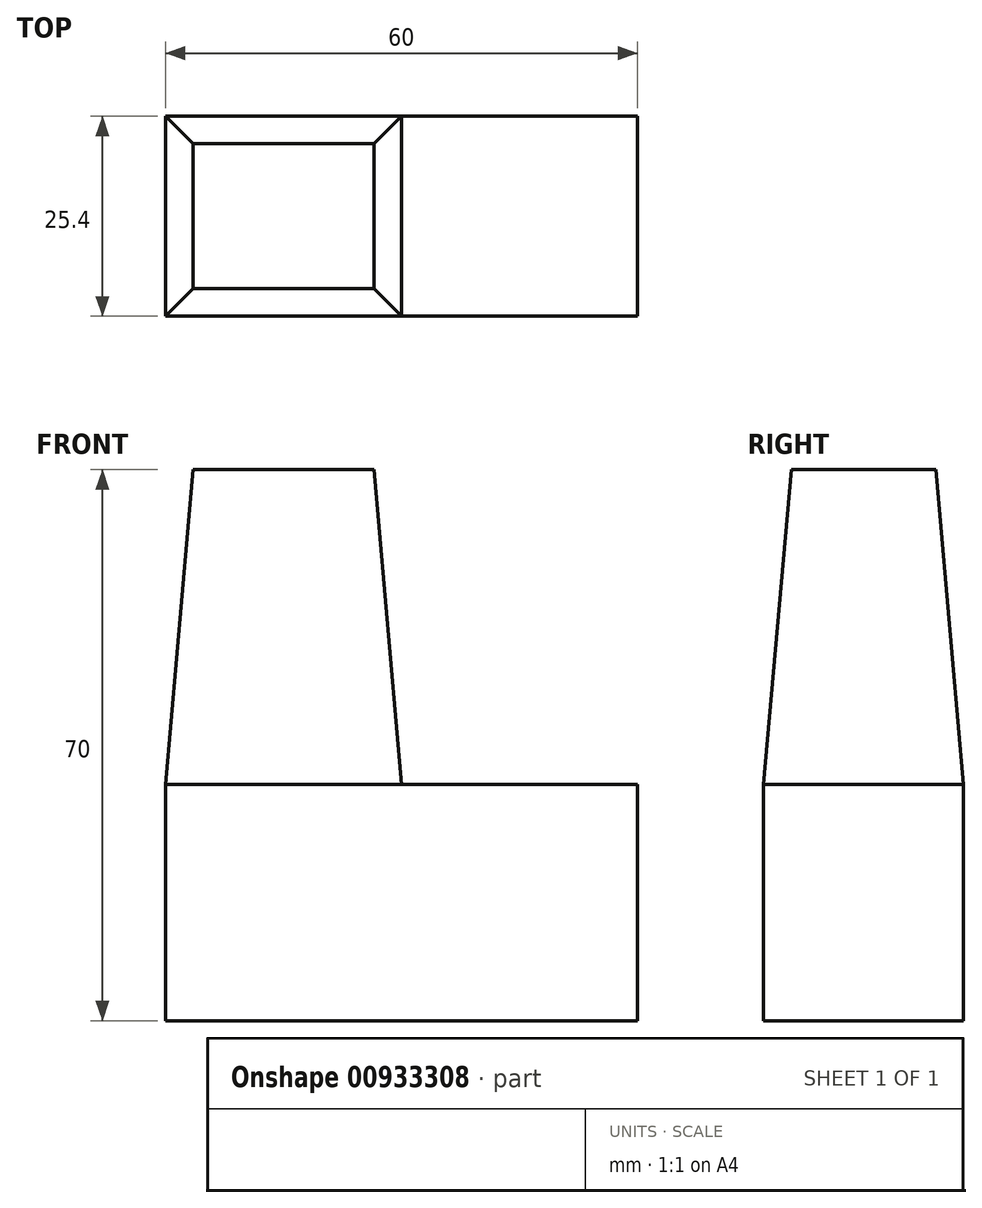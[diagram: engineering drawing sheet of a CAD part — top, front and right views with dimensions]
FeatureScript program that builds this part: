
annotation { "Feature Type Name" : "Feature", "Feature Type Description" : "" }
export const myFeature = defineFeature(function(context is Context, id is Id, definition is map)
    precondition{}
    {
        {
            var Q0;
            Q0=qCreatedBy(makeId("Front.planeOp"),FACE);
            var sketch = newSketch(context, id + "F0", { "sketchPlane" : qUnion([Q0])});
            skLineSegment(sketch, "E0.bottom", {"start": v(-40.67, 0) * mm, "end": v(19.33, 0) * mm});
            skLineSegment(sketch, "E0.top", {"start": v(-40.67, -30) * mm, "end": v(19.33, -30) * mm});
            skLineSegment(sketch, "E0.left", {"start": v(-40.67, 0) * mm, "end": v(-40.67, -30) * mm});
            skLineSegment(sketch, "E0.right", {"start": v(19.33, 0) * mm, "end": v(19.33, -30) * mm});
            skSolve(sketch);
        }
        {
            var Q0;
            Q0=makeQuery(id+"F0.imprint","IMPRINT",FACE,{"disambiguationData":[TD([[makeQuery(id+"F0.imprint","IMPRINT",EDGE,{"derivedFrom":sQuery(id+"F0.wireOp",EDGE,"E0.bottom")}),-1.0]])]});
            extrude(context, id + "F1", {"entities" : qUnion([Q0]), "depth" : 25.4 * mm, "offsetDistance" : 25.4 * mm});
        }
        {
            var Q0;
            Q0=makeQuery(id+"F1.opExtrude","SWEPT_FACE",FACE,{"disambiguationData":[OSD([sQuery(id+"F0.wireOp",EDGE,"E0.bottom")])]});
            var sketch = newSketch(context, id + "F2", { "sketchPlane" : qUnion([Q0])});
            skLineSegment(sketch, "E1.bottom", {"start": v(-40.67, 0) * mm, "end": v(-10.67, 0) * mm});
            skLineSegment(sketch, "E1.top", {"start": v(-40.67, -25.4) * mm, "end": v(-10.67, -25.4) * mm});
            skLineSegment(sketch, "E1.left", {"start": v(-40.67, 0) * mm, "end": v(-40.67, -25.4) * mm});
            skLineSegment(sketch, "E1.right", {"start": v(-10.67, 0) * mm, "end": v(-10.67, -25.4) * mm});
            skSolve(sketch);
        }
        {
            var Q0;
            Q0=makeQuery(id+"F2.imprint","IMPRINT",FACE,{"disambiguationData":[TD([[makeQuery(id+"F2.imprint","IMPRINT",EDGE,{"derivedFrom":sQuery(id+"F2.wireOp",EDGE,"E1.bottom")}),-1.0]])]});
            extrude(context, id + "F3", {"entities" : qUnion([Q0]), "operationType" : NewBodyOperationType.ADD, "depth" : 40 * mm, "offsetDistance" : 25.4 * mm, "hasDraft" : true, "draftAngle" : 5 * degree, "draftPullDirection" : true});
        }
    });
